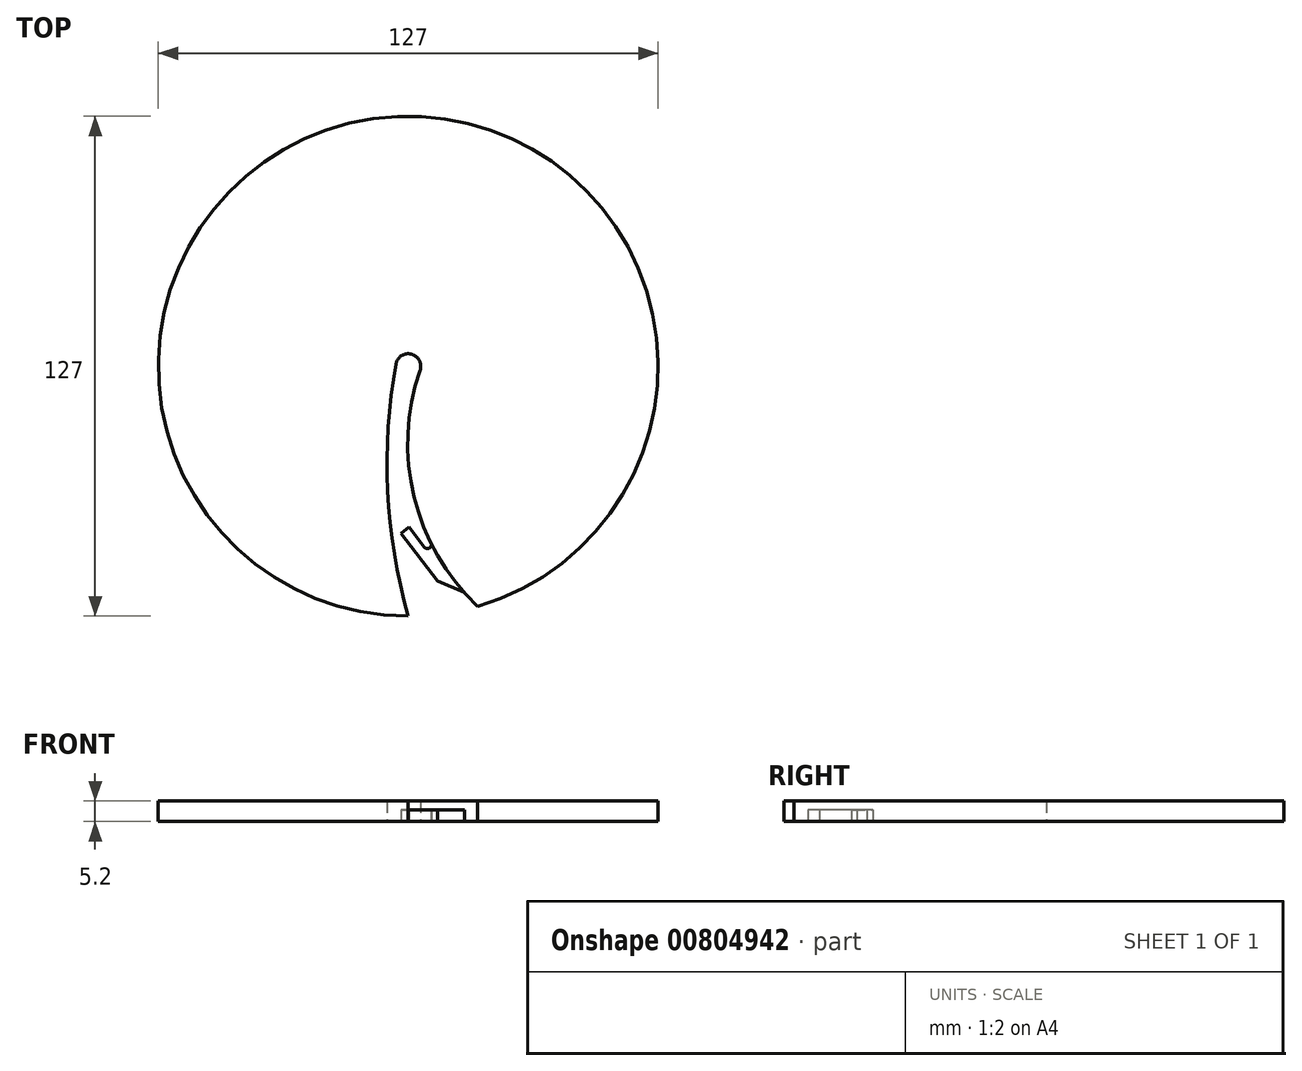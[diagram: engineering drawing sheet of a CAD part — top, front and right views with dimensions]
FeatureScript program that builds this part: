
annotation { "Feature Type Name" : "Feature", "Feature Type Description" : "" }
export const myFeature = defineFeature(function(context is Context, id is Id, definition is map)
    precondition{}
    {
        {
            var Q0;
            Q0=qCreatedBy(makeId("Top.planeOp"),FACE);
            var sketch = newSketch(context, id + "F0", { "sketchPlane" : qUnion([Q0])});
            skArc(sketch, "E0", {"start": v(17.64, -61) * mm, "mid": v(-8.9, 62.87) * mm, "end": v(0, -63.5) * mm});
            skArc(sketch, "E1", {"start": v(3, -1.04) * mm, "mid": v(0.8, 3.07) * mm, "end": v(-3.13, 0.56) * mm});
            skArc(sketch, "E2", {"start": v(-3.13, 0.56) * mm, "mid": v(-5.2, -31.65) * mm, "end": v(0, -63.5) * mm});
            skArc(sketch, "E3", {"start": v(3, -1.04) * mm, "mid": v(1.5, -33.17) * mm, "end": v(17.64, -61) * mm});
            skSolve(sketch);
        }
        {
            var Q0;
            Q0 = qSketchRegion(id + "F0", true);
            extrude(context, id + "F1", {"entities" : qUnion([Q0]), "depth" : 3.2 * mm, "offsetDistance" : 25.4 * mm});
        }
        {
            var Q0;
            {var subQ0=sQuery(id+"F0.wireOp",EDGE,"E3");var subQ1=sQuery(id+"F0.wireOp",EDGE,"E2");var subQ2=sQuery(id+"F0.wireOp",EDGE,"E1");var subQ3=sQuery(id+"F0.wireOp",EDGE,"E0");Q0=makeQuery(id+"FQLvzE7cNwsK4xG_1.boolean.opBoolean","MERGE",FACE,{"derivedFrom":[makeQuery(id+"F1.opExtrude","CAP_FACE",FACE,{"disambiguationData":[OSD([subQ3,subQ2,subQ1,subQ0])],"isStart":true}),makeQuery(id+"FQLvzE7cNwsK4xG_1.opExtrude","CAP_FACE",FACE,{"disambiguationData":[OSD([subQ3,subQ2,subQ1,subQ0])],"isStart":false})]});}
            var sketch = newSketch(context, id + "F2", { "sketchPlane" : qUnion([Q0])});
            skArc(sketch, "E4.0", {"start": v(17.64, 61) * mm, "mid": v(-8.9, -62.87) * mm, "end": v(0, 63.5) * mm});
            skArc(sketch, "E4.1", {"start": v(3, 1.04) * mm, "mid": v(0.8, -3.07) * mm, "end": v(-3.13, -0.56) * mm});
            skArc(sketch, "E4.2", {"start": v(-3.13, -0.56) * mm, "mid": v(-5.2, 31.65) * mm, "end": v(0, 63.5) * mm});
            skArc(sketch, "E4.3", {"start": v(3, 1.04) * mm, "mid": v(1.5, 33.17) * mm, "end": v(17.64, 61) * mm});
            skSolve(sketch);
        }
        {
            var Q0;
            Q0 = qSketchRegion(id + "F2", true);
            extrude(context, id + "F3", {"entities" : qUnion([Q0]), "operationType" : NewBodyOperationType.ADD, "depth" : 2 * mm, "offsetDistance" : 25.4 * mm});
        }
        {
            var Q0;
            Q0=makeQuery(id+"F3.opExtrude","CAP_FACE",FACE,{"disambiguationData":[OSD([sQuery(id+"F2.wireOp",EDGE,"E4.0"),sQuery(id+"F2.wireOp",EDGE,"E4.1"),sQuery(id+"F2.wireOp",EDGE,"E4.2"),sQuery(id+"F2.wireOp",EDGE,"E4.3")])],"isStart":false});
            var sketch = newSketch(context, id + "F4", { "sketchPlane" : qUnion([Q0])});
            skPoint(sketch, "E5.0.start.orphan", {"position": v(-3.13, -0.56) * mm});
            skLineSegment(sketch, "E6", {"start": v(4.07, 45.95) * mm, "end": v(0.23, 40.9) * mm});
            skLineSegment(sketch, "E7", {"start": v(0.23, 40.9) * mm, "end": v(-1.8, 42.44) * mm});
            skLineSegment(sketch, "E8", {"start": v(-1.8, 42.44) * mm, "end": v(7.42, 54.54) * mm});
            skLineSegment(sketch, "E9", {"start": v(7.42, 54.54) * mm, "end": v(14.24, 57.5) * mm});
            skArc(sketch, "E10.0", {"start": v(5.8, 44.98) * mm, "mid": v(9.6, 51.52) * mm, "end": v(14.24, 57.5) * mm});
            skPoint(sketch, "E11.orphan", {"position": v(3, 1.04) * mm});
            skPoint(sketch, "E12.orphan", {"position": v(17.64, 61) * mm});
            skArc(sketch, "E13.filletArc", {"start": v(5.8, 44.98) * mm, "mid": v(5.36, 46.22) * mm, "end": v(4.07, 45.95) * mm});
            skSolve(sketch);
        }
        {
            var Q0;
            Q0 = qSketchRegion(id + "F4", true);
            var Q1;
            {var subQ1=sQuery(id+"F4.wireOp",EDGE,"oCVWX4LY-WVts-enud-uut1-SlNTo9koMmSs");Q1=makeQuery(id+"F4.imprint","IMPRINT",FACE,{"disambiguationData":[TD([[makeQuery(id+"F4.imprint","IMPRINT",EDGE,{"derivedFrom":subQ1}),-1.0]])]});}
            extrude(context, id + "F5", {"entities" : qUnion([Q0, Q1]), "operationType" : NewBodyOperationType.ADD, "oppositeDirection" : true, "depth" : 3 * mm, "offsetDistance" : 25.4 * mm});
        }
    });
